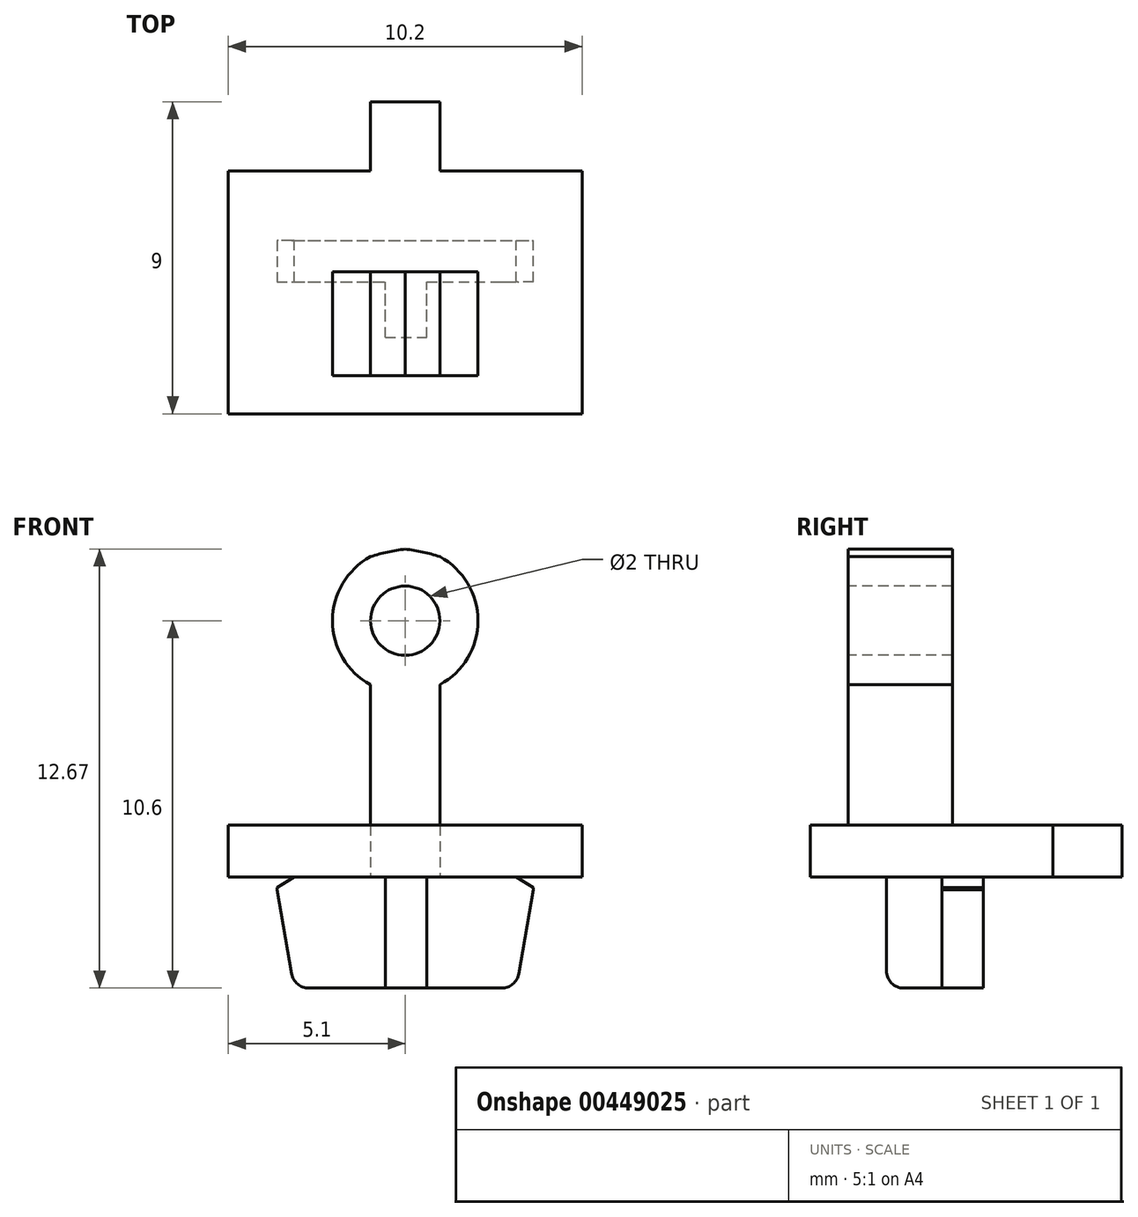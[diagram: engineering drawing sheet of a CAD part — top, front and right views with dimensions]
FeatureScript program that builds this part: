
annotation { "Feature Type Name" : "Feature", "Feature Type Description" : "" }
export const myFeature = defineFeature(function(context is Context, id is Id, definition is map)
    precondition{}
    {
        {
            var Q0;
            Q0=qCreatedBy(makeId("Top.planeOp"),FACE);
            var sketch = newSketch(context, id + "F0", { "sketchPlane" : qUnion([Q0])});
            skLineSegment(sketch, "E0.bottom", {"start": v(0, 0) * mm, "end": v(10.2, 0) * mm});
            skLineSegment(sketch, "E0.top", {"start": v(0, 7) * mm, "end": v(10.2, 7) * mm});
            skLineSegment(sketch, "E0.left", {"start": v(0, 0) * mm, "end": v(0, 7) * mm});
            skLineSegment(sketch, "E0.right", {"start": v(10.2, 0) * mm, "end": v(10.2, 7) * mm});
            skLineSegment(sketch, "E1.bottom", {"start": v(4.1, 7) * mm, "end": v(6.1, 7) * mm});
            skLineSegment(sketch, "E1.top", {"start": v(4.1, 9) * mm, "end": v(6.1, 9) * mm});
            skLineSegment(sketch, "E1.left", {"start": v(4.1, 7) * mm, "end": v(4.1, 9) * mm});
            skLineSegment(sketch, "E1.right", {"start": v(6.1, 7) * mm, "end": v(6.1, 9) * mm});
            skSolve(sketch);
        }
        {
            var Q0;
            Q0 = qSketchRegion(id + "F0", true);
            extrude(context, id + "F1", {"entities" : qUnion([Q0]), "depth" : 1.5 * mm});
        }
        {
            var Q0;
            Q0=makeQuery(id+"F1.opExtrude","CAP_FACE",FACE,{"disambiguationData":[OSD([sQuery(id+"F0.wireOp",EDGE,"E0.bottom"),sQuery(id+"F0.wireOp",EDGE,"E0.top"),sQuery(id+"F0.wireOp",EDGE,"E0.left"),sQuery(id+"F0.wireOp",EDGE,"E0.right"),sQuery(id+"F0.wireOp",EDGE,"E1.top"),sQuery(id+"F0.wireOp",EDGE,"E1.left"),sQuery(id+"F0.wireOp",EDGE,"E1.right")])],"isStart":true});
            var sketch = newSketch(context, id + "F2", { "sketchPlane" : qUnion([Q0])});
            skLineSegment(sketch, "E2.bottom", {"start": v(1.4, -3.8) * mm, "end": v(8.8, -3.8) * mm});
            skLineSegment(sketch, "E2.top", {"start": v(1.4, -5) * mm, "end": v(8.8, -5) * mm});
            skLineSegment(sketch, "E2.left", {"start": v(1.4, -3.8) * mm, "end": v(1.4, -5) * mm});
            skLineSegment(sketch, "E2.right", {"start": v(8.8, -3.8) * mm, "end": v(8.8, -5) * mm});
            skLineSegment(sketch, "E3.bottom", {"start": v(4.52, -2.2) * mm, "end": v(5.72, -2.2) * mm});
            skLineSegment(sketch, "E3.top", {"start": v(4.52, -4.8) * mm, "end": v(5.72, -4.8) * mm});
            skLineSegment(sketch, "E3.left", {"start": v(4.52, -2.2) * mm, "end": v(4.52, -4.8) * mm});
            skLineSegment(sketch, "E3.right", {"start": v(5.72, -2.2) * mm, "end": v(5.72, -4.8) * mm});
            skSolve(sketch);
        }
        {
            var Q0;
            Q0 = qSketchRegion(id + "F2", true);
            extrude(context, id + "F3", {"entities" : qUnion([Q0]), "operationType" : NewBodyOperationType.ADD, "depth" : 3.2 * mm});
        }
        {
            var Q0;
            {var subQ0=sQuery(id+"F2.wireOp",EDGE,"E2.top");Q0=makeQuery(id+"F3.opExtrude","SWEPT_FACE",FACE,{"disambiguationData":[OSD([subQ0]),TDD([makeQuery(id+"F2.imprint","IMPRINT",EDGE,{"disambiguationData":[TD([[makeQuery(id+"F2.imprint","INTERSECT",VERTEX,{"derivedFrom":[subQ0,sQuery(id+"F2.wireOp",EDGE,"E2.left")]}),-1.0]])],"derivedFrom":subQ0})])]});}
            var sketch = newSketch(context, id + "F4", { "sketchPlane" : qUnion([Q0])});
            skLineSegment(sketch, "E4", {"start": v(-1.4, 0) * mm, "end": v(-1.9, 0) * mm});
            skLineSegment(sketch, "E5", {"start": v(-1.9, 0) * mm, "end": v(-1.4, -0.3) * mm});
            skLineSegment(sketch, "E6", {"start": v(-1.4, -0.3) * mm, "end": v(-1.4, 0) * mm});
            skSolve(sketch);
        }
        {
            var Q0;
            Q0 = qSketchRegion(id + "F4", true);
            extrude(context, id + "F5", {"entities" : qUnion([Q0]), "operationType" : NewBodyOperationType.REMOVE, "oppositeDirection" : true, "depth" : 25 * mm});
        }
        {
            var Q0;
            {var subQ0=sQuery(id+"F2.wireOp",EDGE,"E2.top");Q0=makeQuery(id+"F3.opExtrude","SWEPT_FACE",FACE,{"disambiguationData":[OSD([subQ0]),TDD([makeQuery(id+"F2.imprint","IMPRINT",EDGE,{"disambiguationData":[TD([[makeQuery(id+"F2.imprint","INTERSECT",VERTEX,{"derivedFrom":[subQ0,sQuery(id+"F2.wireOp",EDGE,"E2.right")]}),1.0]])],"derivedFrom":subQ0})])]});}
            var sketch = newSketch(context, id + "F6", { "sketchPlane" : qUnion([Q0])});
            skLineSegment(sketch, "E7", {"start": v(-8.8, 0) * mm, "end": v(-8.3, 0) * mm});
            skLineSegment(sketch, "E8", {"start": v(-8.3, 0) * mm, "end": v(-8.8, -0.3) * mm});
            skLineSegment(sketch, "E9", {"start": v(-8.8, -0.3) * mm, "end": v(-8.8, 0) * mm});
            skSolve(sketch);
        }
        {
            var Q0;
            Q0 = qSketchRegion(id + "F6", true);
            extrude(context, id + "F7", {"entities" : qUnion([Q0]), "operationType" : NewBodyOperationType.REMOVE, "oppositeDirection" : true, "depth" : 25 * mm});
        }
        {
            var Q0;
            Q0=makeQuery(id+"F3.opExtrude","CAP_EDGE",EDGE,{"disambiguationData":[OSD([sQuery(id+"F2.wireOp",EDGE,"E2.left")])],"isStart":false});
            chamfer(context, id + "F8", {"entities" : qUnion([Q0]), "chamferType" : ChamferType.OFFSET_ANGLE, "width" : 0.5 * mm, "oppositeDirection" : false, "angle" : 80 * degree});
        }
        {
            var Q0;
            Q0=makeQuery(id+"F3.opExtrude","CAP_EDGE",EDGE,{"disambiguationData":[OSD([sQuery(id+"F2.wireOp",EDGE,"E2.right")])],"isStart":false});
            chamfer(context, id + "F9", {"entities" : qUnion([Q0]), "chamferType" : ChamferType.OFFSET_ANGLE, "width" : 0.5 * mm, "oppositeDirection" : true, "angle" : 80 * degree, "tangentPropagation" : true});
        }
        {
            var Q0;
            Q0=makeQuery(id+"F3.opExtrude","CAP_EDGE",EDGE,{"disambiguationData":[OSD([sQuery(id+"F2.wireOp",EDGE,"E3.bottom")])],"isStart":false});
            var Q1;
            Q1=makeQuery(id+"F3.opExtrude","CAP_EDGE",EDGE,{"disambiguationData":[OSD([sQuery(id+"F2.wireOp",EDGE,"E3.top")])],"isStart":false});
            var Q2;
            {var subQ0=sQuery(id+"F2.wireOp",EDGE,"E2.right");Q2=makeQuery(id+"F9.opChamfer","BLEND_EDGE",EDGE,{"blendedFrom":[makeQuery(id+"F3.opExtrude","CAP_EDGE",EDGE,{"disambiguationData":[OSD([subQ0])],"isStart":false}),makeQuery(id+"F3.opExtrude","CAP_FACE",FACE,{"disambiguationData":[OSD([sQuery(id+"F2.wireOp",EDGE,"E2.bottom"),sQuery(id+"F2.wireOp",EDGE,"E2.top"),sQuery(id+"F2.wireOp",EDGE,"E2.left"),subQ0,sQuery(id+"F2.wireOp",EDGE,"E3.bottom"),sQuery(id+"F2.wireOp",EDGE,"E3.top"),sQuery(id+"F2.wireOp",EDGE,"E3.left"),sQuery(id+"F2.wireOp",EDGE,"E3.right")])],"isStart":false})],"blendedInto":[makeQuery(id+"F3.opExtrude","CAP_FACE",FACE,{"disambiguationData":[OSD([sQuery(id+"F2.wireOp",EDGE,"E2.bottom"),sQuery(id+"F2.wireOp",EDGE,"E2.top"),sQuery(id+"F2.wireOp",EDGE,"E2.left"),subQ0,sQuery(id+"F2.wireOp",EDGE,"E3.bottom"),sQuery(id+"F2.wireOp",EDGE,"E3.top"),sQuery(id+"F2.wireOp",EDGE,"E3.left"),sQuery(id+"F2.wireOp",EDGE,"E3.right")])],"isStart":false})]});}
            var Q3;
            {var subQ0=sQuery(id+"F2.wireOp",EDGE,"E2.left");Q3=makeQuery(id+"F8.opChamfer","BLEND_EDGE",EDGE,{"blendedFrom":[makeQuery(id+"F3.opExtrude","CAP_EDGE",EDGE,{"disambiguationData":[OSD([subQ0])],"isStart":false}),makeQuery(id+"F3.opExtrude","CAP_FACE",FACE,{"disambiguationData":[OSD([sQuery(id+"F2.wireOp",EDGE,"E2.bottom"),sQuery(id+"F2.wireOp",EDGE,"E2.top"),subQ0,sQuery(id+"F2.wireOp",EDGE,"E2.right"),sQuery(id+"F2.wireOp",EDGE,"E3.bottom"),sQuery(id+"F2.wireOp",EDGE,"E3.top"),sQuery(id+"F2.wireOp",EDGE,"E3.left"),sQuery(id+"F2.wireOp",EDGE,"E3.right")])],"isStart":false})],"blendedInto":[makeQuery(id+"F3.opExtrude","CAP_FACE",FACE,{"disambiguationData":[OSD([sQuery(id+"F2.wireOp",EDGE,"E2.bottom"),sQuery(id+"F2.wireOp",EDGE,"E2.top"),subQ0,sQuery(id+"F2.wireOp",EDGE,"E2.right"),sQuery(id+"F2.wireOp",EDGE,"E3.bottom"),sQuery(id+"F2.wireOp",EDGE,"E3.top"),sQuery(id+"F2.wireOp",EDGE,"E3.left"),sQuery(id+"F2.wireOp",EDGE,"E3.right")])],"isStart":false})]});}
            fillet(context, id + "F10", {"entities" : qUnion([Q0, Q1, Q2, Q3]), "radius" : 0.5 * mm, "tangentPropagation" : true, "allowEdgeOverflow" : false});
        }
        {
            var Q0;
            Q0=makeQuery(id+"F1.opExtrude","CAP_FACE",FACE,{"disambiguationData":[OSD([sQuery(id+"F0.wireOp",EDGE,"E0.bottom"),sQuery(id+"F0.wireOp",EDGE,"E0.top"),sQuery(id+"F0.wireOp",EDGE,"E0.left"),sQuery(id+"F0.wireOp",EDGE,"E0.right"),sQuery(id+"F0.wireOp",EDGE,"E1.top"),sQuery(id+"F0.wireOp",EDGE,"E1.left"),sQuery(id+"F0.wireOp",EDGE,"E1.right")])],"isStart":false});
            var sketch = newSketch(context, id + "F11", { "sketchPlane" : qUnion([Q0])});
            skLineSegment(sketch, "E10.bottom", {"start": v(4.1, 4.1) * mm, "end": v(6.1, 4.1) * mm});
            skLineSegment(sketch, "E10.top", {"start": v(4.1, 1.1) * mm, "end": v(6.1, 1.1) * mm});
            skLineSegment(sketch, "E10.left", {"start": v(4.1, 4.1) * mm, "end": v(4.1, 1.1) * mm});
            skLineSegment(sketch, "E10.right", {"start": v(6.1, 4.1) * mm, "end": v(6.1, 1.1) * mm});
            skSolve(sketch);
        }
        {
            var Q0;
            Q0 = qSketchRegion(id + "F11", true);
            extrude(context, id + "F12", {"entities" : qUnion([Q0]), "operationType" : NewBodyOperationType.ADD, "depth" : 8 * mm});
        }
        {
            var Q0;
            Q0=makeQuery(id+"F12.opExtrude","SWEPT_FACE",FACE,{"disambiguationData":[OSD([sQuery(id+"F11.wireOp",EDGE,"E10.top")])]});
            var sketch = newSketch(context, id + "F13", { "sketchPlane" : qUnion([Q0])});
            skCircle(sketch, "E11", {"center": v(5.1, 7.4) * mm, "radius": 2.1 * mm});
            skSolve(sketch);
        }
        {
            var Q0;
            Q0 = qSketchRegion(id + "F13", true);
            extrude(context, id + "F14", {"entities" : qUnion([Q0]), "operationType" : NewBodyOperationType.ADD, "oppositeDirection" : true, "depth" : 3 * mm});
        }
        {
            var Q0;
            Q0=makeQuery(id+"F12.opExtrude","CAP_EDGE",EDGE,{"disambiguationData":[OSD([sQuery(id+"F11.wireOp",EDGE,"E10.left")])],"isStart":false});
            var Q1;
            Q1=makeQuery(id+"F12.opExtrude","CAP_EDGE",EDGE,{"disambiguationData":[OSD([sQuery(id+"F11.wireOp",EDGE,"E10.right")])],"isStart":false});
            fillet(context, id + "F15", {"entities" : qUnion([Q0, Q1]), "radius" : 5 * mm, "tangentPropagation" : true, "allowEdgeOverflow" : false});
        }
        {
            var Q0;
            Q0=makeQuery(id+"F14.boolean.opBoolean","MERGE",FACE,{"derivedFrom":[makeQuery(id+"F12.opExtrude","SWEPT_FACE",FACE,{"disambiguationData":[OSD([sQuery(id+"F11.wireOp",EDGE,"E10.top")])]}),makeQuery(id+"F14.opExtrude","CAP_FACE",FACE,{"disambiguationData":[OSD([sQuery(id+"F13.wireOp",EDGE,"E11")])],"isStart":true})]});
            var sketch = newSketch(context, id + "F16", { "sketchPlane" : qUnion([Q0])});
            skCircle(sketch, "E12", {"center": v(5.1, 7.4) * mm, "radius": 1 * mm});
            skSolve(sketch);
        }
        {
            var Q0;
            Q0 = qSketchRegion(id + "F16", true);
            extrude(context, id + "F17", {"entities" : qUnion([Q0]), "operationType" : NewBodyOperationType.REMOVE, "oppositeDirection" : true, "depth" : 25 * mm});
        }
    });
